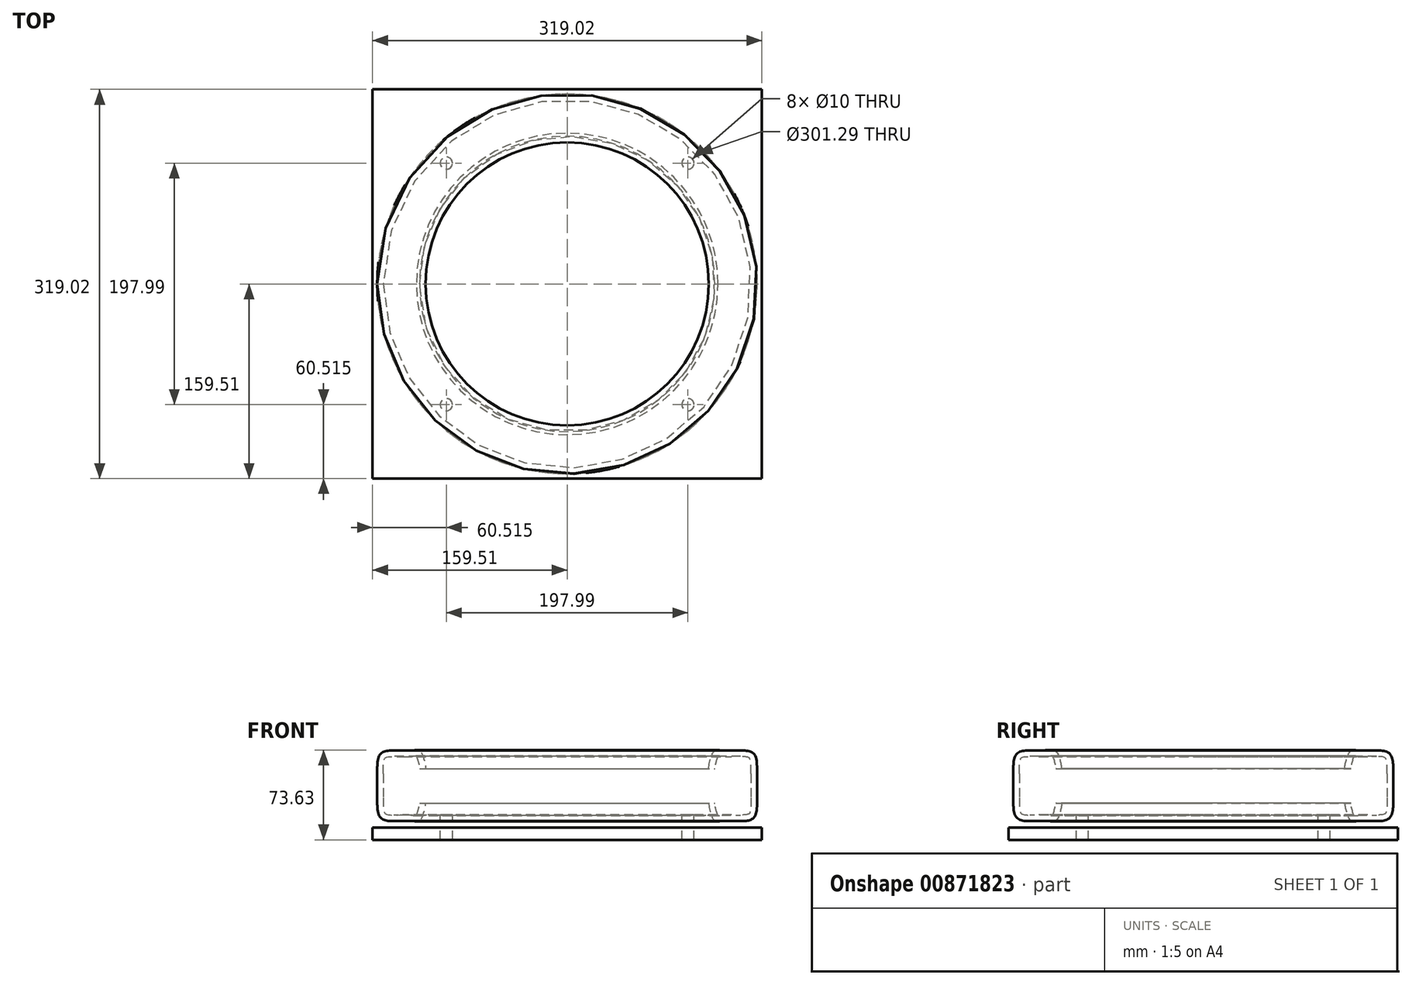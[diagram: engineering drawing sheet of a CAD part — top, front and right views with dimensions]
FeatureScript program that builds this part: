
annotation { "Feature Type Name" : "Feature", "Feature Type Description" : "" }
export const myFeature = defineFeature(function(context is Context, id is Id, definition is map)
    precondition{}
    {
        {
            var Q0;
            Q0=qCreatedBy(makeId("Front.planeOp"),FACE);
            var sketch = newSketch(context, id + "F0", { "sketchPlane" : qUnion([Q0])});
            skLineSegment(sketch, "E0", {"start": v(0, 34.3) * mm, "end": v(84.19, 34.3) * mm, "construction": true});
            skLineSegment(sketch, "E1", {"start": v(155.64, 34.3) * mm, "end": v(155.64, 24.55) * mm});
            skFitSpline(sketch, "E2", {"points": [v(155.64, 24.55) * mm, v(153.8, 9.3) * mm, v(145.17, 5.4) * mm, v(132.4, 5.4) * mm, v(121.68, 5.4) * mm, v(118.33, 9.62) * mm, v(115.99, 20.19) * mm], "startDerivative": vector(0, -65.82) * mm, "endDerivative": vector(0, 47.61) * mm});
            skLineSegment(sketch, "E3", {"start": v(115.99, 20.19) * mm, "end": v(115.99, 34.3) * mm});
            skLineSegment(sketch, "E4.MirrorCS", {"start": v(115.99, 48.42) * mm, "end": v(115.99, 34.3) * mm});
            skLineSegment(sketch, "E5.MirrorCS", {"start": v(155.64, 34.3) * mm, "end": v(155.64, 44.05) * mm});
            skFitSpline(sketch, "E6.MirrorCS", {"points": [v(155.64, 44.05) * mm, v(153.8, 59.3) * mm, v(145.17, 63.2) * mm, v(132.4, 63.2) * mm, v(121.68, 63.2) * mm, v(118.33, 58.98) * mm, v(115.99, 48.42) * mm], "startDerivative": vector(0, 65.82) * mm, "endDerivative": vector(0, -47.61) * mm});
            skLineSegment(sketch, "E7", {"start": v(0, 0) * mm, "end": v(0, 118.1) * mm});
            skSolve(sketch);
        }
        {
            var Q0;
            Q0=qCreatedBy(makeId("Front.planeOp"),FACE);
            var sketch = newSketch(context, id + "F1", { "sketchPlane" : qUnion([Q0])});
            skLineSegment(sketch, "E8", {"start": v(0, 0) * mm, "end": v(0, 168.93) * mm, "construction": true});
            skSolve(sketch);
        }
        {
            var Q0;
            Q0=makeQuery(id+"F0.imprint","IMPRINT",FACE,{"disambiguationData":[TD([[makeQuery(id+"F0.imprint","IMPRINT",EDGE,{"derivedFrom":sQuery(id+"F0.wireOp",EDGE,"E1")}),-1.0]])]});
            var Q1;
            Q1=sQuery(id+"F1.wireOp",EDGE,"E8");
            revolve(context, id + "F2", {"surfaceOperationType" : NewSurfaceOperationType.NEW, "entities" : qUnion([Q0]), "axis" : qUnion([Q1]), "revolveType" : RevolveType.FULL});
        }
        {
            var Q0;
            Q0=makeQuery(id+"F2.opRevolve","SWEPT_FACE",FACE,{"disambiguationData":[OSD([sQuery(id+"F0.wireOp",EDGE,"E3"),sQuery(id+"F0.wireOp",EDGE,"E4.MirrorCS")])]});
            shell(context, id + "F3", {"entities" : qUnion([Q0]), "thickness" : 5 * mm});
        }
        {
            var Q0;
            Q0=qCreatedBy(makeId("Top.planeOp"),FACE);
            var sketch = newSketch(context, id + "F4", { "sketchPlane" : qUnion([Q0])});
            skLineSegment(sketch, "E9.bottom", {"start": v(159.5, -159.5) * mm, "end": v(-159.5, -159.5) * mm});
            skLineSegment(sketch, "E9.top", {"start": v(159.5, 159.5) * mm, "end": v(-159.5, 159.5) * mm});
            skLineSegment(sketch, "E9.left", {"start": v(159.5, -159.5) * mm, "end": v(159.5, 159.5) * mm});
            skLineSegment(sketch, "E9.right", {"start": v(-159.5, -159.5) * mm, "end": v(-159.5, 159.5) * mm});
            skPoint(sketch, "E9.middle", {"position": v(0, 0) * mm});
            skSolve(sketch);
        }
        {
            var Q0;
            Q0 = qSketchRegion(id + "F4", true);
            extrude(context, id + "F5", {"entities" : qUnion([Q0]), "oppositeDirection" : true, "depth" : 10 * mm, "offsetDistance" : 25.4 * mm});
        }
        {
            var Q0;
            Q0=makeQuery(id+"F5.opExtrude","CAP_FACE",FACE,{"disambiguationData":[OSD([sQuery(id+"F4.wireOp",EDGE,"E9.bottom"),sQuery(id+"F4.wireOp",EDGE,"E9.top"),sQuery(id+"F4.wireOp",EDGE,"E9.left"),sQuery(id+"F4.wireOp",EDGE,"E9.right")])],"isStart":true});
            var sketch = newSketch(context, id + "F6", { "sketchPlane" : qUnion([Q0])});
            skCircle(sketch, "E10", {"center": v(0, 0) * mm, "radius": 140 * mm, "construction": true});
            skCircle(sketch, "E11", {"center": v(99, -99) * mm, "radius": 5 * mm});
            skLineSegment(sketch, "E12", {"start": v(0, 0) * mm, "end": v(159.5, -159.5) * mm, "construction": true});
            skCircle(sketch, "E13.1.0", {"center": v(99, 99) * mm, "radius": 5 * mm});
            skCircle(sketch, "E13.2.0", {"center": v(-99, 99) * mm, "radius": 5 * mm});
            skCircle(sketch, "E14.1.3.0", {"center": v(-99, -99) * mm, "radius": 5 * mm});
            skSolve(sketch);
        }
        {
            var Q0;
            Q0 = qSketchRegion(id + "F6", true);
            extrude(context, id + "F7", {"entities" : qUnion([Q0]), "operationType" : NewBodyOperationType.REMOVE, "oppositeDirection" : true, "depth" : 25 * mm, "offsetDistance" : 25 * mm, "hasSecondDirection" : true, "secondDirectionOppositeDirection" : false, "secondDirectionDepth" : 26.9 * mm});
        }
    });
